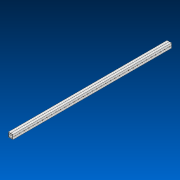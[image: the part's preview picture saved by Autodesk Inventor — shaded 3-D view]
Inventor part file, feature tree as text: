
AUTODESK INVENTOR PART (.ipt)
format: ipt  version: 2022.2 (Build 262287000, 287)  size: 792,064 bytes
history: native  units: in
note: dims shown in document units (in); Inventor stores cm internally (conversion verified against a paired STEP export)
features: other x35, extrude x1, pattern_linear x1, sketch x1, pattern_circular x1
ambient origin geometry x8: Origin, YZ Plane, XZ Plane, XY Plane, X Axis, Y Axis, Z Axis, Center Point
bodies: Solid1 (feature_tree)
feature tree (39):
  extrude  "Extrusion1"  Depth=1.0in
  other  "Work Axis1"
  pattern_linear  "Rectangular Pattern1"  Spacing1=0.0in  [1 undecoded]
  sketch  "Sketch1"  dims[d0=1.0in d1=24.0in d2=0.0in d3=13.7795in d5=1.0in]
  other  "Work Axis2"
  other  "Work Axis3"
  other  "Work Axis4"
  other  "Work Axis5"
  other  "Work Axis6"
  other  "Work Axis7"
  other  "Work Axis8"
  other  "Work Axis9"
  other  "Work Axis10"
  other  "Work Axis11"
  other  "Work Axis12"
  other  "Work Axis13"
  other  "Work Axis14"
  other  "Work Axis15"
  other  "Work Axis16"
  other  "Work Axis17"
  other  "Work Axis18"
  other  "Work Axis19"
  other  "Work Axis20"
  other  "Work Axis21"
  other  "Work Axis22"
  other  "Work Axis23"
  other  "Work Axis24"
  other  "Work Axis25"
  other  "Work Axis26"
  other  "Work Axis27"
  other  "Work Axis28"
  other  "Work Axis29"
  other  "Work Axis30"
  other  "Work Axis31"
  other  "Work Axis32"
  other  "Work Axis33"
  other  "Work Axis34"
  other  "Work Axis35"
  pattern_circular  "CirPattern2"
note: 1 required parameter value undecoded (feature->parameter linkage not recoverable at this tier; creation-order binding heuristic only, values carry confidence <= 0.55)
